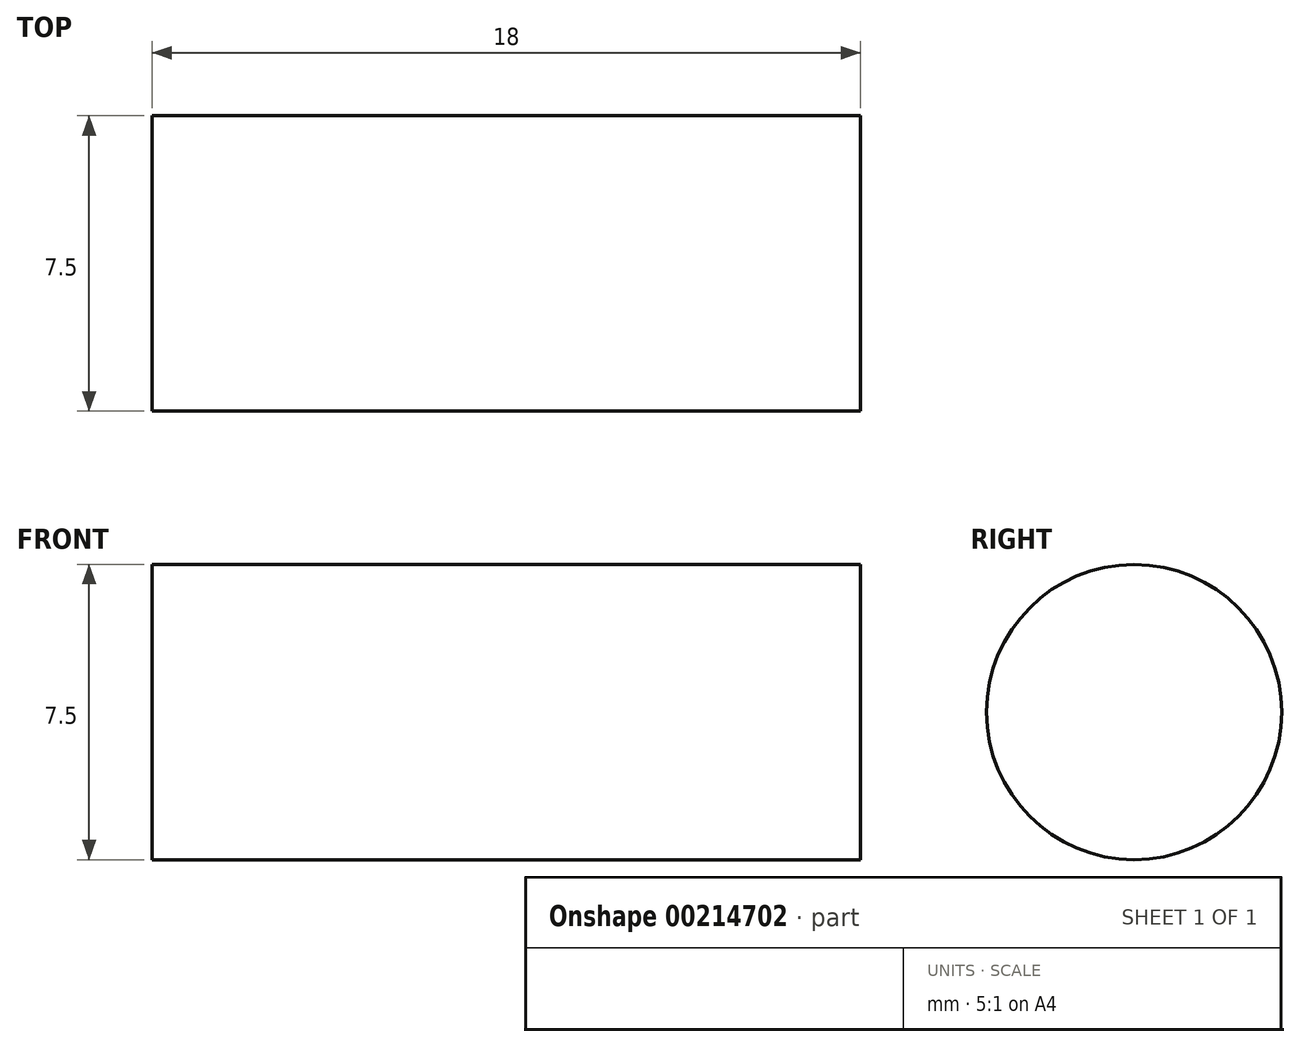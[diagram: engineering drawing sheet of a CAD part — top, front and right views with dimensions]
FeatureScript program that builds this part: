
annotation { "Feature Type Name" : "Feature", "Feature Type Description" : "" }
export const myFeature = defineFeature(function(context is Context, id is Id, definition is map)
    precondition{}
    {
        {
            var Q0;
            Q0=qCreatedBy(makeId("Right.planeOp"),FACE);
            var sketch = newSketch(context, id + "F0", { "sketchPlane" : qUnion([Q0])});
            skCircle(sketch, "E0", {"center": v(0, 0) * mm, "radius": 3.75 * mm});
            skSolve(sketch);
        }
        {
            var Q0;
            Q0 = qSketchRegion(id + "F0", true);
            extrude(context, id + "F1", {"entities" : qUnion([Q0]), "depth" : 18 * mm});
        }
    });
